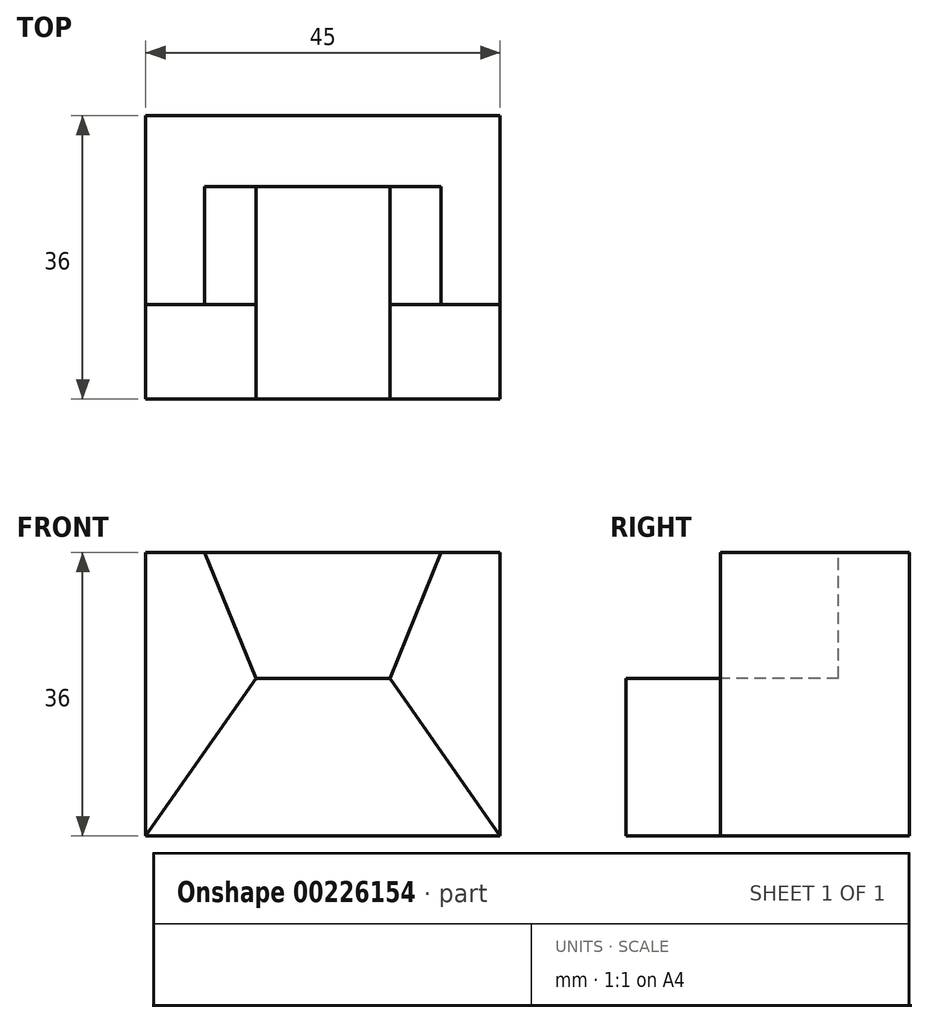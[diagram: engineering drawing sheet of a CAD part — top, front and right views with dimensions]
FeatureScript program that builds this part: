
annotation { "Feature Type Name" : "Feature", "Feature Type Description" : "" }
export const myFeature = defineFeature(function(context is Context, id is Id, definition is map)
    precondition{}
    {
        {
            var Q0;
            Q0=qCreatedBy(makeId("Front.planeOp"),FACE);
            var sketch = newSketch(context, id + "F0", { "sketchPlane" : qUnion([Q0])});
            skLineSegment(sketch, "E0.bottom", {"start": v(0, 0) * mm, "end": v(45, 0) * mm});
            skLineSegment(sketch, "E0.top", {"start": v(0, 36) * mm, "end": v(45, 36) * mm});
            skLineSegment(sketch, "E0.left", {"start": v(0, 0) * mm, "end": v(0, 36) * mm});
            skLineSegment(sketch, "E0.right", {"start": v(45, 0) * mm, "end": v(45, 36) * mm});
            skLineSegment(sketch, "E1", {"start": v(14, 20) * mm, "end": v(31, 20) * mm});
            skLineSegment(sketch, "E2", {"start": v(31, 20) * mm, "end": v(37.5, 36) * mm});
            skLineSegment(sketch, "E3", {"start": v(31, 20) * mm, "end": v(45, 0) * mm});
            skLineSegment(sketch, "E4", {"start": v(22.5, 36) * mm, "end": v(22.5, 0) * mm, "construction": true});
            skLineSegment(sketch, "E5.MirrorCS", {"start": v(14, 20) * mm, "end": v(7.5, 36) * mm});
            skLineSegment(sketch, "E6.MirrorCS", {"start": v(14, 20) * mm, "end": v(0, 0) * mm});
            skSolve(sketch);
        }
        {
            var Q0;
            {var subQ0=sQuery(id+"F0.wireOp",EDGE,"E0.left");Q0=makeQuery(id+"F0.imprint","IMPRINT",FACE,{"disambiguationData":[TD([[makeQuery(id+"F0.imprint","IMPRINT",EDGE,{"derivedFrom":subQ0}),-1.0]])]});}
            var Q1;
            Q1=makeQuery(id+"F0.imprint","IMPRINT",FACE,{"disambiguationData":[TD([[makeQuery(id+"F0.imprint","IMPRINT",EDGE,{"derivedFrom":sQuery(id+"F0.wireOp",EDGE,"E1")}),1.0]])]});
            var Q2;
            {var subQ0=sQuery(id+"F0.wireOp",EDGE,"E0.right");Q2=makeQuery(id+"F0.imprint","IMPRINT",FACE,{"disambiguationData":[TD([[makeQuery(id+"F0.imprint","IMPRINT",EDGE,{"derivedFrom":subQ0}),1.0]])]});}
            var Q3;
            Q3=makeQuery(id+"F0.imprint","IMPRINT",FACE,{"disambiguationData":[TD([[makeQuery(id+"F0.imprint","IMPRINT",EDGE,{"derivedFrom":sQuery(id+"F0.wireOp",EDGE,"E0.bottom")}),1.0]])]});
            extrude(context, id + "F1", {"entities" : qUnion([Q0, Q1, Q2, Q3]), "oppositeDirection" : true, "depth" : 24 * mm});
        }
        {
            var Q0;
            Q0=makeQuery(id+"F0.imprint","IMPRINT",FACE,{"disambiguationData":[TD([[makeQuery(id+"F0.imprint","IMPRINT",EDGE,{"derivedFrom":sQuery(id+"F0.wireOp",EDGE,"E1")}),1.0]])]});
            extrude(context, id + "F2", {"entities" : qUnion([Q0]), "operationType" : NewBodyOperationType.REMOVE, "oppositeDirection" : true, "depth" : (24 - 9) * mm});
        }
        {
            var Q0;
            Q0=makeQuery(id+"F0.imprint","IMPRINT",FACE,{"disambiguationData":[TD([[makeQuery(id+"F0.imprint","IMPRINT",EDGE,{"derivedFrom":sQuery(id+"F0.wireOp",EDGE,"E0.bottom")}),1.0]])]});
            extrude(context, id + "F3", {"entities" : qUnion([Q0]), "operationType" : NewBodyOperationType.ADD, "depth" : (36 - 24) * mm});
        }
    });
